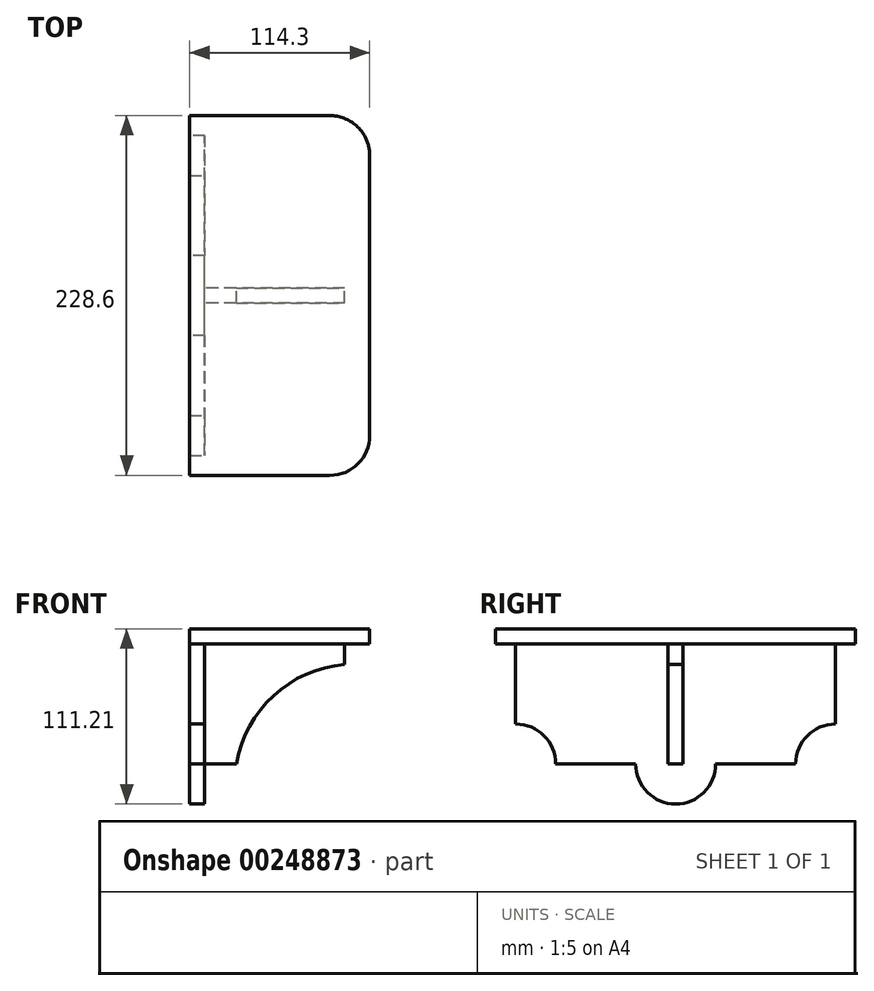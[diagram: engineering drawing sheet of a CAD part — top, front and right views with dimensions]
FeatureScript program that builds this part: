
annotation { "Feature Type Name" : "Feature", "Feature Type Description" : "" }
export const myFeature = defineFeature(function(context is Context, id is Id, definition is map)
    precondition{}
    {
        {
            var Q0;
            Q0=qCreatedBy(makeId("Right.planeOp"),FACE);
            var sketch = newSketch(context, id + "F0", { "sketchPlane" : qUnion([Q0])});
            skLineSegment(sketch, "E0", {"start": v(-104.08, 34.48) * mm, "end": v(99.12, 34.48) * mm});
            skLineSegment(sketch, "E1", {"start": v(99.12, 34.48) * mm, "end": v(99.12, -41.72) * mm});
            skLineSegment(sketch, "E2", {"start": v(99.12, -41.72) * mm, "end": v(-104.08, -41.72) * mm});
            skLineSegment(sketch, "E3", {"start": v(-104.08, -41.72) * mm, "end": v(-104.08, 34.48) * mm});
            skLineSegment(sketch, "E4", {"start": v(-104.08, 34.48) * mm, "end": v(-104.08, 44) * mm});
            skLineSegment(sketch, "E5", {"start": v(-104.08, 44) * mm, "end": v(99.12, 44) * mm});
            skLineSegment(sketch, "E6", {"start": v(99.12, 44) * mm, "end": v(99.12, 34.48) * mm});
            skPoint(sketch, "E7", {"position": v(-2.48, -41.72) * mm});
            skArc(sketch, "E8", {"start": v(-27.88, -41.72) * mm, "mid": v(-2.48, -67.12) * mm, "end": v(22.92, -41.72) * mm});
            skLineSegment(sketch, "E9", {"start": v(99.12, 34.48) * mm, "end": v(111.82, 34.48) * mm});
            skLineSegment(sketch, "E10", {"start": v(111.82, 34.48) * mm, "end": v(111.82, 44.09) * mm});
            skLineSegment(sketch, "E11", {"start": v(111.82, 44.09) * mm, "end": v(99.12, 44) * mm});
            skLineSegment(sketch, "E12", {"start": v(-104.08, 44) * mm, "end": v(-116.78, 44) * mm});
            skLineSegment(sketch, "E13", {"start": v(-116.78, 44) * mm, "end": v(-116.78, 34.48) * mm});
            skLineSegment(sketch, "E14", {"start": v(-116.78, 34.48) * mm, "end": v(-104.08, 34.48) * mm});
            skSolve(sketch);
        }
        {
            var Q0;
            Q0=makeQuery(id+"F0.imprint","IMPRINT",FACE,{"disambiguationData":[TD([[makeQuery(id+"F0.imprint","IMPRINT",EDGE,{"derivedFrom":sQuery(id+"F0.wireOp",EDGE,"E0")}),1.0]])]});
            var Q1;
            Q1=makeQuery(id+"F0.imprint","IMPRINT",FACE,{"disambiguationData":[TD([[makeQuery(id+"F0.imprint","IMPRINT",EDGE,{"derivedFrom":sQuery(id+"F0.wireOp",EDGE,"E6")}),1.0]])]});
            var Q2;
            Q2=makeQuery(id+"F0.imprint","IMPRINT",FACE,{"disambiguationData":[TD([[makeQuery(id+"F0.imprint","IMPRINT",EDGE,{"derivedFrom":sQuery(id+"F0.wireOp",EDGE,"E4")}),1.0]])]});
            extrude(context, id + "F1", {"entities" : qUnion([Q0, Q1, Q2]), "depth" : 114.3 * mm});
        }
        {
            var Q0;
            Q0=makeQuery(id+"F0.imprint","IMPRINT",FACE,{"disambiguationData":[TD([[makeQuery(id+"F0.imprint","IMPRINT",EDGE,{"derivedFrom":sQuery(id+"F0.wireOp",EDGE,"E0")}),-1.0]])]});
            var Q1;
            {var subQ0=sQuery(id+"F0.wireOp",EDGE,"E8");Q1=makeQuery(id+"F0.imprint","IMPRINT",FACE,{"disambiguationData":[TD([[makeQuery(id+"F0.imprint","IMPRINT",EDGE,{"derivedFrom":subQ0}),1.0]])]});}
            extrude(context, id + "F2", {"entities" : qUnion([Q0, Q1]), "operationType" : NewBodyOperationType.ADD, "depth" : 9.52 * mm});
        }
        {
            var Q0;
            Q0=makeQuery(id+"F2.opExtrude","CAP_FACE",FACE,{"disambiguationData":[OSD([sQuery(id+"F0.wireOp",EDGE,"E0"),sQuery(id+"F0.wireOp",EDGE,"E1"),sQuery(id+"F0.wireOp",EDGE,"E2"),sQuery(id+"F0.wireOp",EDGE,"E3"),sQuery(id+"F0.wireOp",EDGE,"E8")])],"isStart":false});
            var sketch = newSketch(context, id + "F3", { "sketchPlane" : qUnion([Q0])});
            skPoint(sketch, "E15", {"position": v(-2.48, 34.48) * mm});
            skLineSegment(sketch, "E16.0", {"start": v(-104.08, 40.83) * mm, "end": v(99.12, 40.83) * mm});
            skLineSegment(sketch, "E17", {"start": v(-7.25, 34.48) * mm, "end": v(-7.25, -41.72) * mm});
            skLineSegment(sketch, "E18", {"start": v(2.28, 34.48) * mm, "end": v(2.28, -41.72) * mm});
            skLineSegment(sketch, "E19", {"start": v(-7.25, 34.48) * mm, "end": v(2.28, 34.48) * mm});
            skLineSegment(sketch, "E20", {"start": v(-7.25, -41.72) * mm, "end": v(2.28, -41.72) * mm});
            skSolve(sketch);
        }
        {
            var Q0;
            Q0=makeQuery(id+"F3.imprint","IMPRINT",FACE,{"disambiguationData":[TD([[makeQuery(id+"F3.imprint","IMPRINT",EDGE,{"derivedFrom":sQuery(id+"F3.wireOp",EDGE,"E17")}),1.0]])]});
            extrude(context, id + "F4", {"entities" : qUnion([Q0]), "operationType" : NewBodyOperationType.ADD, "depth" : 88.9 * mm});
        }
        {
            var Q0;
            Q0=makeQuery(id+"F4.opExtrude","SWEPT_FACE",FACE,{"disambiguationData":[OSD([sQuery(id+"F3.wireOp",EDGE,"E18")])]});
            var sketch = newSketch(context, id + "F5", { "sketchPlane" : qUnion([Q0])});
            skLineSegment(sketch, "E21", {"start": v(-98.43, 21.78) * mm, "end": v(-9.52, 21.78) * mm});
            skLineSegment(sketch, "E22", {"start": v(-28.58, 21.78) * mm, "end": v(-28.57, -41.72) * mm});
            skCircle(sketch, "E23", {"center": v(-104.78, -54.42) * mm, "radius": 76.2 * mm});
            skSolve(sketch);
        }
        {
            var Q0;
            {var subQ0=sQuery(id+"F5.wireOp",EDGE,"E23");var subQ1=sQuery(id+"F3.wireOp",EDGE,"E18");var subQ4=makeQuery(id+"F4.opExtrude","CAP_EDGE",EDGE,{"disambiguationData":[OSD([subQ1])],"isStart":false});var subQ5=makeQuery(id+"F5.imprint","INTERSECT",VERTEX,{"derivedFrom":[subQ4,subQ0]});Q0=makeQuery(id+"F5.imprint","IMPRINT",FACE,{"disambiguationData":[TD([[makeQuery(id+"F5.imprint","IMPRINT",EDGE,{"disambiguationData":[TD([[subQ5,1.0]])],"derivedFrom":subQ0}),1.0]])]});}
            extrude(context, id + "F6", {"entities" : qUnion([Q0]), "operationType" : NewBodyOperationType.REMOVE, "endBound" : BoundingType.THROUGH_ALL, "oppositeDirection" : true, "depth" : 25.4 * mm});
        }
        {
            var Q0;
            Q0=makeQuery(id+"F2.opExtrude","CAP_FACE",FACE,{"disambiguationData":[OSD([sQuery(id+"F0.wireOp",EDGE,"E0"),sQuery(id+"F0.wireOp",EDGE,"E1"),sQuery(id+"F0.wireOp",EDGE,"E2"),sQuery(id+"F0.wireOp",EDGE,"E3"),sQuery(id+"F0.wireOp",EDGE,"E8")])],"isStart":false});
            var sketch = newSketch(context, id + "F7", { "sketchPlane" : qUnion([Q0])});
            skCircle(sketch, "E24", {"center": v(99.12, -41.72) * mm, "radius": 25.4 * mm});
            skCircle(sketch, "E25", {"center": v(-104.08, -41.72) * mm, "radius": 25.4 * mm});
            skSolve(sketch);
        }
        {
            var Q0;
            {var subQ0=sQuery(id+"F7.wireOp",EDGE,"E25");var subQ1=sQuery(id+"F0.wireOp",EDGE,"E3");var subQ5=makeQuery(id+"F2.opExtrude","CAP_EDGE",EDGE,{"disambiguationData":[OSD([subQ1])],"isStart":false});var subQ6=makeQuery(id+"F7.imprint","INTERSECT",VERTEX,{"derivedFrom":[subQ5,subQ0]});Q0=makeQuery(id+"F7.imprint","IMPRINT",FACE,{"disambiguationData":[TD([[makeQuery(id+"F7.imprint","IMPRINT",EDGE,{"disambiguationData":[TD([[subQ6,1.0]])],"derivedFrom":subQ0}),1.0]])]});}
            var Q1;
            {var subQ0=sQuery(id+"F7.wireOp",EDGE,"E24");var subQ1=sQuery(id+"F0.wireOp",EDGE,"E1");var subQ2=makeQuery(id+"F2.opExtrude","CAP_EDGE",EDGE,{"disambiguationData":[OSD([subQ1])],"isStart":false});var subQ3=makeQuery(id+"F7.imprint","INTERSECT",VERTEX,{"derivedFrom":[subQ2,subQ0]});Q1=makeQuery(id+"F7.imprint","IMPRINT",FACE,{"disambiguationData":[TD([[makeQuery(id+"F7.imprint","IMPRINT",EDGE,{"disambiguationData":[TD([[subQ3,-1.0]])],"derivedFrom":subQ0}),1.0]])]});}
            extrude(context, id + "F8", {"entities" : qUnion([Q0, Q1]), "operationType" : NewBodyOperationType.REMOVE, "endBound" : BoundingType.THROUGH_ALL, "oppositeDirection" : true, "depth" : 25.4 * mm});
        }
        {
            var Q0;
            Q0=makeQuery(id+"F1.opExtrude","SWEPT_FACE",FACE,{"disambiguationData":[OSD([sQuery(id+"F0.wireOp",EDGE,"E0"),sQuery(id+"F0.wireOp",EDGE,"E9"),sQuery(id+"F0.wireOp",EDGE,"E14")])]});
            var sketch = newSketch(context, id + "F9", { "sketchPlane" : qUnion([Q0])});
            skLineSegment(sketch, "E26", {"start": v(114.3, -82.58) * mm, "end": v(114.3, -86.42) * mm});
            skLineSegment(sketch, "E27", {"start": v(95.89, -111.82) * mm, "end": v(88.9, -111.82) * mm});
            skLineSegment(sketch, "E28", {"start": v(114.3, 87.29) * mm, "end": v(114.3, 91.38) * mm});
            skLineSegment(sketch, "E29", {"start": v(89.58, 116.78) * mm, "end": v(88.9, 116.78) * mm});
            skPoint(sketch, "E30.visualSharp", {"position": v(114.3, 116.78) * mm});
            skArc(sketch, "E30.filletArc", {"start": v(114.3, 91.38) * mm, "mid": v(106.86, 109.34) * mm, "end": v(88.9, 116.78) * mm});
            skPoint(sketch, "E31.visualSharp", {"position": v(114.3, -111.82) * mm});
            skArc(sketch, "E31.filletArc", {"start": v(88.9, -111.82) * mm, "mid": v(106.86, -104.38) * mm, "end": v(114.3, -86.42) * mm});
            skSolve(sketch);
        }
        {
            var Q0;
            {var subQ0=sQuery(id+"F9.wireOp",EDGE,"E29");Q0=makeQuery(id+"F9.imprint","IMPRINT",FACE,{"disambiguationData":[TD([[makeQuery(id+"F9.imprint","IMPRINT",EDGE,{"derivedFrom":subQ0}),1.0]])]});}
            var Q1;
            {var subQ0=sQuery(id+"F9.wireOp",EDGE,"E27");Q1=makeQuery(id+"F9.imprint","IMPRINT",FACE,{"disambiguationData":[TD([[makeQuery(id+"F9.imprint","IMPRINT",EDGE,{"derivedFrom":subQ0}),-1.0]])]});}
            extrude(context, id + "F10", {"entities" : qUnion([Q0, Q1]), "operationType" : NewBodyOperationType.REMOVE, "endBound" : BoundingType.THROUGH_ALL, "oppositeDirection" : true, "depth" : 25.4 * mm});
        }
    });
